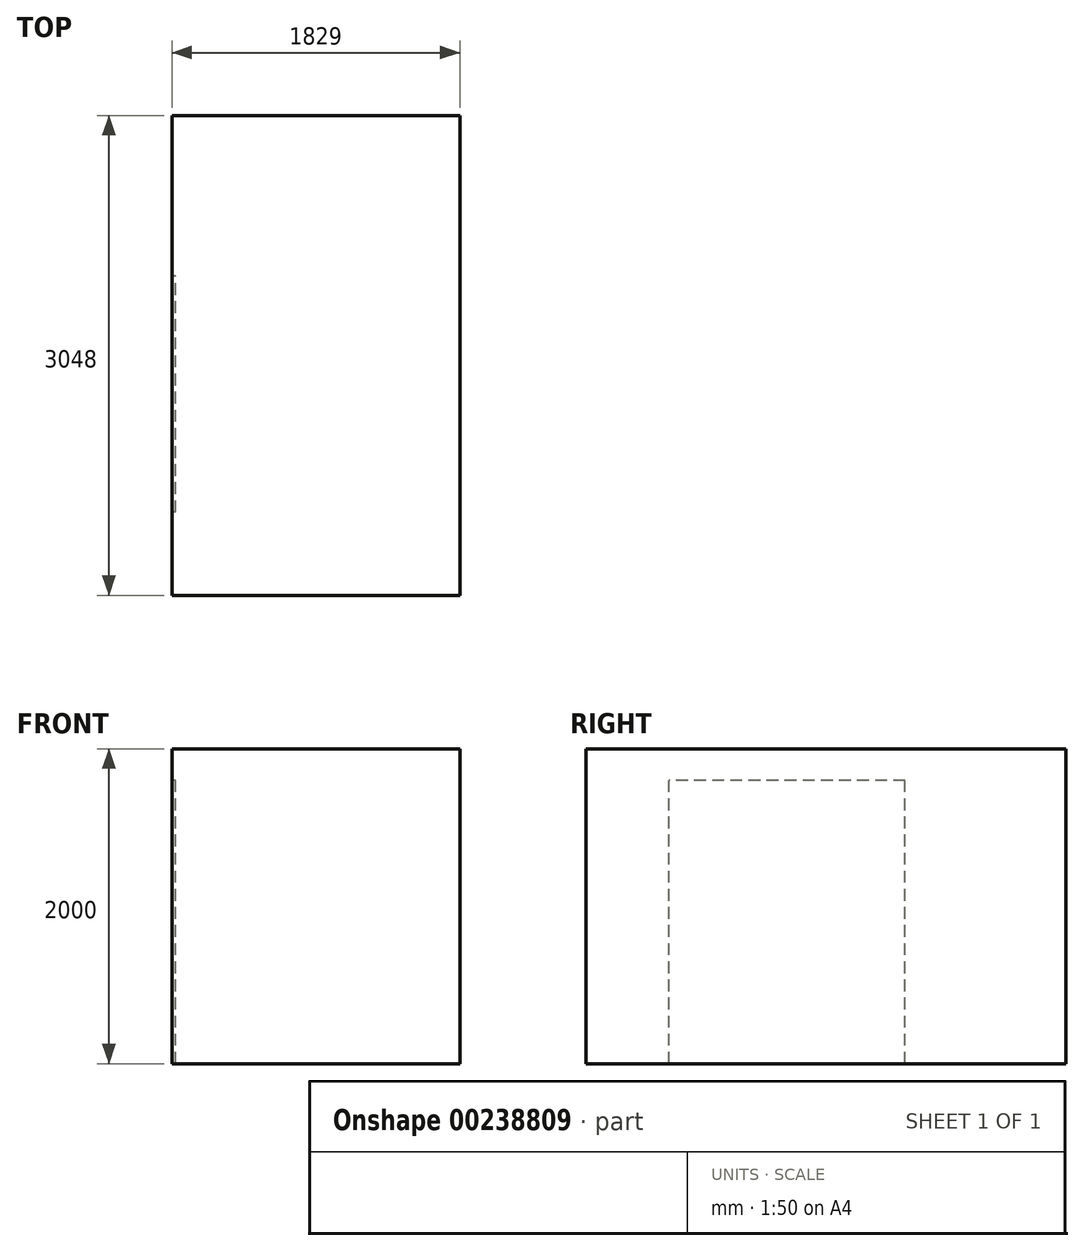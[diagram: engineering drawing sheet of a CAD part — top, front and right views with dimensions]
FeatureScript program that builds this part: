
annotation { "Feature Type Name" : "Feature", "Feature Type Description" : "" }
export const myFeature = defineFeature(function(context is Context, id is Id, definition is map)
    precondition{}
    {
        {
            var Q0;
            Q0=qCreatedBy(makeId("Top.planeOp"),FACE);
            var sketch = newSketch(context, id + "F0", { "sketchPlane" : qUnion([Q0])});
            skLineSegment(sketch, "E0.bottom", {"start": v(0, 0) * mm, "end": v(1829, 0) * mm});
            skLineSegment(sketch, "E0.top", {"start": v(0, 3048) * mm, "end": v(1829, 3048) * mm});
            skLineSegment(sketch, "E0.left", {"start": v(0, 0) * mm, "end": v(0, 3048) * mm});
            skLineSegment(sketch, "E0.right", {"start": v(1829, 0) * mm, "end": v(1829, 3048) * mm});
            skSolve(sketch);
        }
        {
            var Q0;
            Q0 = qSketchRegion(id + "F0", true);
            extrude(context, id + "F1", {"entities" : qUnion([Q0]), "depth" : 2000 * mm});
        }
        {
            var Q0;
            Q0=makeQuery(id+"F1.opExtrude","SWEPT_FACE",FACE,{"disambiguationData":[OSD([sQuery(id+"F0.wireOp",EDGE,"E0.left")])]});
            var sketch = newSketch(context, id + "F2", { "sketchPlane" : qUnion([Q0])});
            skLineSegment(sketch, "E1.bottom", {"start": v(-2028.21, 0) * mm, "end": v(-528.21, 0) * mm});
            skLineSegment(sketch, "E1.top", {"start": v(-2028.21, 1800) * mm, "end": v(-528.21, 1800) * mm});
            skLineSegment(sketch, "E1.left", {"start": v(-2028.21, 0) * mm, "end": v(-2028.21, 1800) * mm});
            skLineSegment(sketch, "E1.right", {"start": v(-528.21, 0) * mm, "end": v(-528.21, 1800) * mm});
            skSolve(sketch);
        }
        {
            var Q0;
            Q0 = qSketchRegion(id + "F2", true);
            extrude(context, id + "F3", {"entities" : qUnion([Q0]), "operationType" : NewBodyOperationType.REMOVE, "oppositeDirection" : true, "depth" : 25 * mm});
        }
    });
